SOLIDWORKS PART (.sldprt)
format: sldprt  version: not decoded by parser v0  size: 115,200 bytes
history: native  units: mm
features: plane x3, sketch x3, material x1, revolve x1, extrude x1, cut_extrude x1, chamfer x1 (+10 scaffold rows collapsed)
feature tree (21):
  scaffold x10  (default folders/planes/origin — collapsed)
  material  "Matériau <non spécifié>"
  plane  "Plan de face"
  plane  "Plan de dessus"
  plane  "Plan de droite"
  sketch  "Esquisse1"  dims[c1.D1=~11.352469mm c2.D1=135.0deg]
  revolve  "Révolution2"  Angle=360deg
  sketch  "Esquisse3"  dims[D1=~1.457329mm]
  extrude  "Extrusion1"  Depth=13mm
  sketch  "Esquisse2"  dims[D1=0.4mm D2=0.4mm]
  cut_extrude  "Enlèv. mat.-Extru.2"  Depth=1.2mm
  chamfer  "Chanfrein1"  Distance=1.45mm Angle=60deg
decode coverage: 7 of 7 modeling features carry decoded parameters
note: ~ marks probable driven/reference dimensions
note: suppression state not decoded; provenance and decode notes live in map.json
